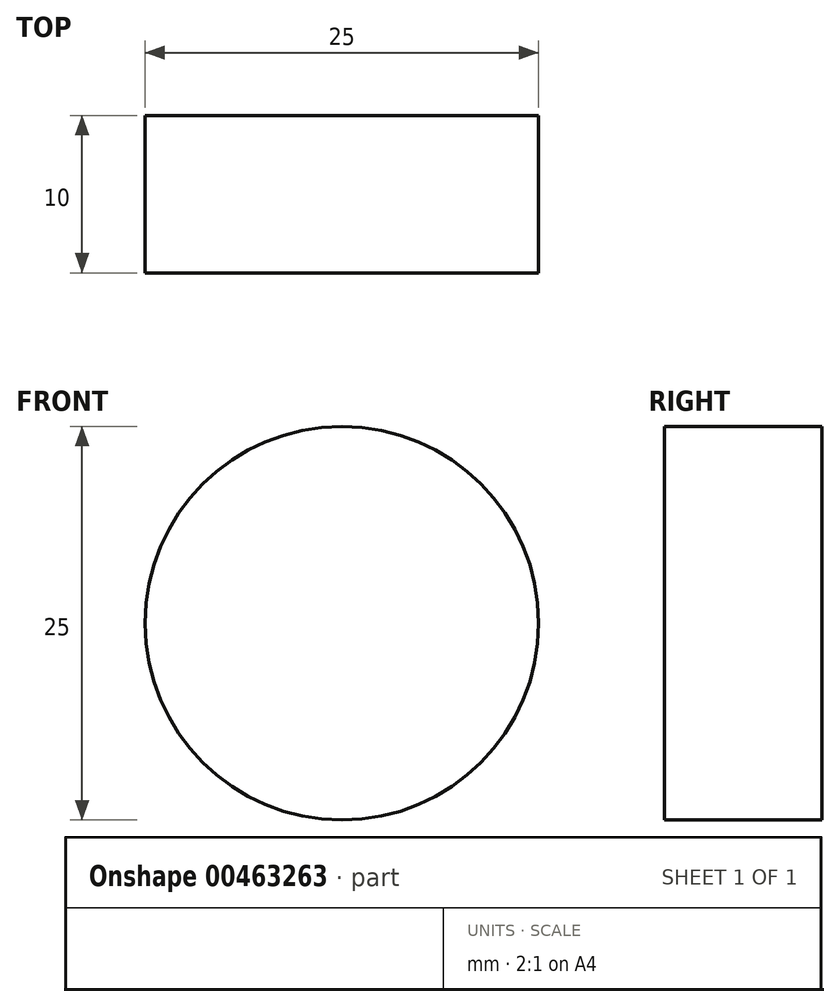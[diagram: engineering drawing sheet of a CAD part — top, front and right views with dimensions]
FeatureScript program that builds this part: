
annotation { "Feature Type Name" : "Feature", "Feature Type Description" : "" }
export const myFeature = defineFeature(function(context is Context, id is Id, definition is map)
    precondition{}
    {
        {
            var Q0;
            Q0=qCreatedBy(makeId("Front.planeOp"),FACE);
            var sketch = newSketch(context, id + "F0", { "sketchPlane" : qUnion([Q0])});
            skCircle(sketch, "E0", {"center": v(0, 0) * mm, "radius": 12.5 * mm});
            skSolve(sketch);
        }
        {
            var Q0;
            Q0 = qSketchRegion(id + "F0", true);
            extrude(context, id + "F1", {"entities" : qUnion([Q0]), "depth" : 10 * mm});
        }
    });
